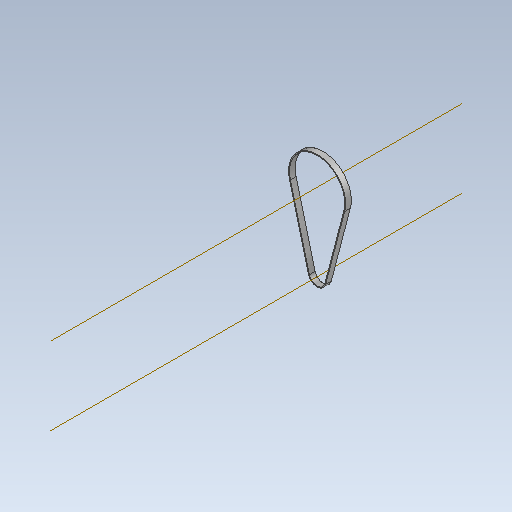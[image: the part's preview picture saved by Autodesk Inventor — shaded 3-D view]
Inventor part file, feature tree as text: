
AUTODESK INVENTOR PART (.ipt)
format: ipt  version: 2020 (Build 240168000, 168)  size: 102,912 bytes
history: native  units: mm (DEFAULTED — no unit token found)
features: other x4, plane x2, sketch x1, sweep x1
ambient origin geometry x8: Origin, YZ Plane, XZ Plane, XY Plane, X Axis, Y Axis, Z Axis, Center Point
bodies: Solid1 (feature_tree)
feature tree (8):
  sketch  "Sketch Path"  dims[d0=4.0mm d2=0.0mm d4=0.3mm d5=0.3mm d6=0.0mm d7=0.0mm d8=0.0mm d9=0.0mm d10=0.0mm d11=0.0mm]
  other  "Cross Section Plane"
  other  "Work Axis1"
  other  "Work Axis2"
  plane  "Work Plane2"
  plane  "Work Plane3"
  sweep  "Belt"
  other  "Cross Section"
